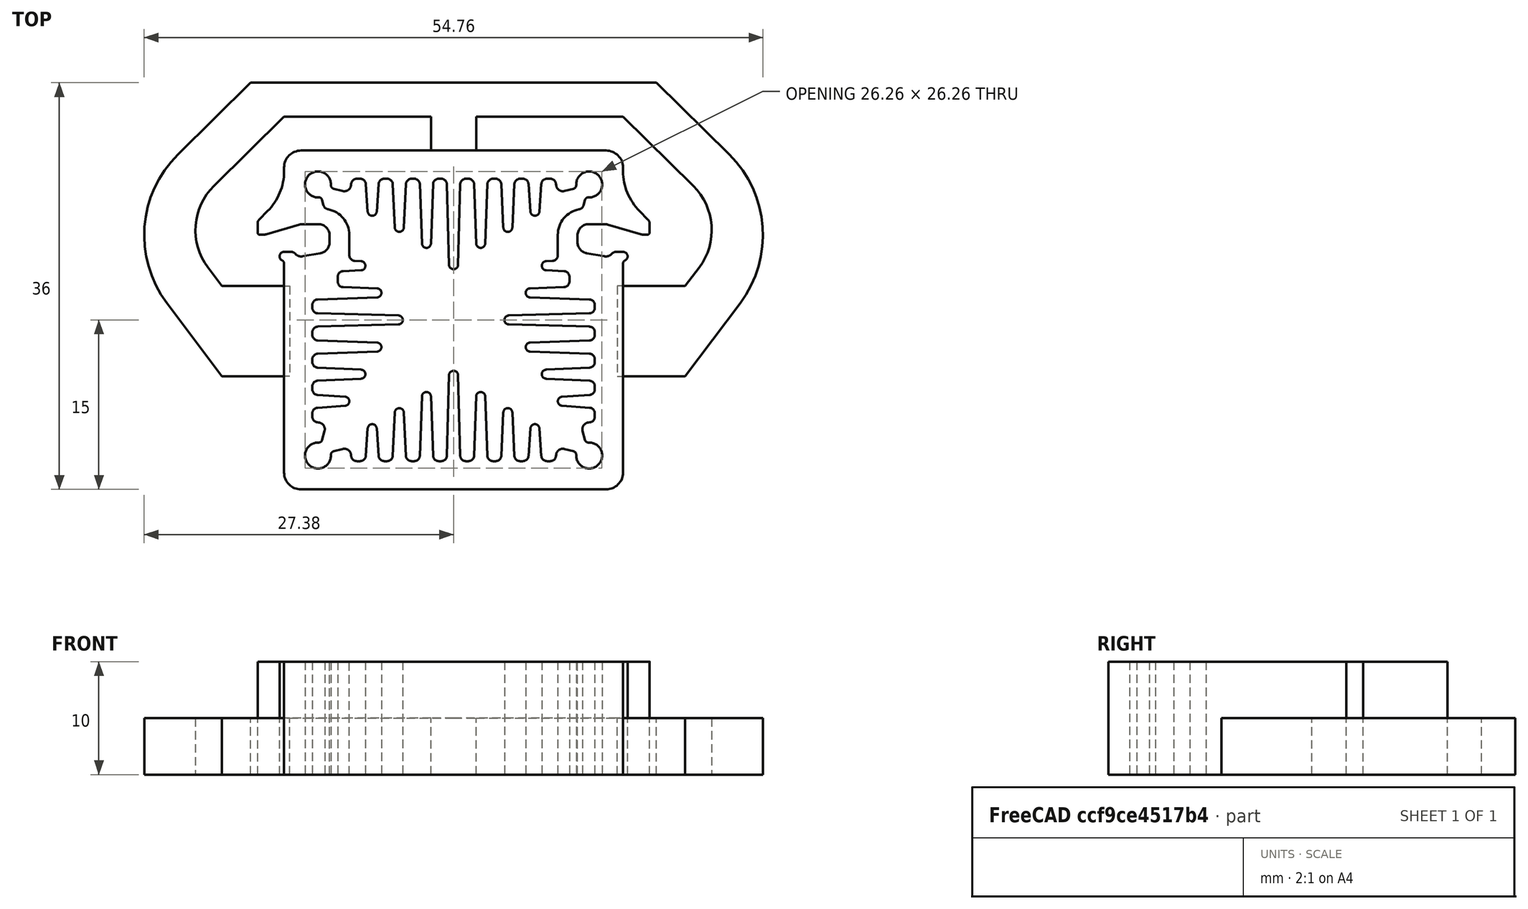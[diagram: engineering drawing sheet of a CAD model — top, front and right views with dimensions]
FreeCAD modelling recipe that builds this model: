
FCSTD DOCUMENT  (FreeCAD 0.20R29603 (Git))
Label: NTCclip
License: All rights reserved
LicenseURL: http://en.wikipedia.org/wiki/All_rights_reserved
objects: Part::Feature×1, Sketcher::SketchObject×1, PartDesign::Pad×1, PartDesign::Body×1
note: 5 computed .brp shape members not serialized (recipe doc carries the construction recipe); baked Part::Feature solids carry a one-line shape summary decoded from their .brp

FEATURE [Part::Feature] Part__Feature  label="LAM_3_K"
  shape: bbox 34.69 x 30 x 10 mm, 252 faces (baked)
FEATURE [Sketcher::SketchObject] Sketch
  FullyConstrained = false
  MapMode = 5
  Support = -> [XY_Plane]
  sketch-geometry (33):
    g0: LineSegment StartX=-14.5 StartY=3 StartZ=0 EndX=-14.5 EndY=-5 EndZ=0
    g1: LineSegment StartX=-14.5 StartY=-5 StartZ=0 EndX=-20.5 EndY=-5 EndZ=0
    g2: LineSegment StartX=-20.5 StartY=-5 StartZ=0 EndX=-25.3698 EndY=1.49312 EndZ=0
    g3: LineSegment StartX=-24.3914 StartY=14.6527 StartZ=0 EndX=-17.9605 EndY=21 EndZ=0
    g4: LineSegment StartX=-17.9605 StartY=21 StartZ=0 EndX=0 EndY=21 EndZ=0
    g5: LineSegment StartX=0 StartY=21 StartZ=0 EndX=0 EndY=15 EndZ=0
    g6: LineSegment StartX=0 StartY=15 StartZ=0 EndX=-2 EndY=15 EndZ=0
    g7: LineSegment StartX=-2 StartY=15 StartZ=0 EndX=-2 EndY=18 EndZ=0
    g8: LineSegment StartX=-2 StartY=18 StartZ=0 EndX=-15 EndY=18 EndZ=0
    g9: LineSegment StartX=-15 StartY=18 StartZ=0 EndX=-21.2076 EndY=11.8731 EndZ=0
    g10: LineSegment StartX=-21.744 StartY=4.65863 StartZ=0 EndX=-20.5 EndY=3 EndZ=0
    g11: LineSegment StartX=-20.5 StartY=3 StartZ=0 EndX=-14.5 EndY=3 EndZ=0
    g12: ArcOfCircle CenterX=-17.344 CenterY=7.95863 CenterZ=0 NormalX=0 NormalY=0 NormalZ=1 AngleXU=0 Radius=5.5 StartAngle=2.34966 EndAngle=3.78509
    g13: GeomPoint X=-24.625 Y=8.5 Z=0
    g14: ArcOfCircle CenterX=-17.344 CenterY=7.51252 CenterZ=0 NormalX=0 NormalY=0 NormalZ=1 AngleXU=0 Radius=10.0323 StartAngle=2.34966 EndAngle=3.78509
    g15: GeomPoint X=-30.625 Y=8.5 Z=0
    g16: LineSegment StartX=-30.625 StartY=8.5 StartZ=0 EndX=-24.625 EndY=8.5 EndZ=0
    g17: LineSegment StartX=14.5 StartY=3 StartZ=0 EndX=14.5 EndY=-5 EndZ=0
    g18: LineSegment StartX=14.5 StartY=-5 StartZ=0 EndX=20.5 EndY=-5 EndZ=0
    g19: LineSegment StartX=20.5 StartY=-5 StartZ=0 EndX=25.3698 EndY=1.49312 EndZ=0
    g20: LineSegment StartX=24.3914 StartY=14.6527 StartZ=0 EndX=17.9605 EndY=21 EndZ=0
    g21: LineSegment StartX=17.9605 StartY=21 StartZ=0 EndX=0 EndY=21 EndZ=0
    g22: LineSegment StartX=-2.372e-12 StartY=15 StartZ=0 EndX=2 EndY=15 EndZ=0
    g23: LineSegment StartX=2 StartY=15 StartZ=0 EndX=2 EndY=18 EndZ=0
    g24: LineSegment StartX=2 StartY=18 StartZ=0 EndX=15 EndY=18 EndZ=0
    g25: LineSegment StartX=15 StartY=18 StartZ=0 EndX=21.2076 EndY=11.8731 EndZ=0
    g26: LineSegment StartX=21.744 StartY=4.65863 StartZ=0 EndX=20.5 EndY=3 EndZ=0
    g27: LineSegment StartX=20.5 StartY=3 StartZ=0 EndX=14.5 EndY=3 EndZ=0
    g28: ArcOfCircle CenterX=17.344 CenterY=7.95863 CenterZ=0 NormalX=0 NormalY=0 NormalZ=1 AngleXU=0 Radius=5.5 StartAngle=5.63968 EndAngle=7.07512
    g29: GeomPoint X=24.625 Y=8.5 Z=0
    g30: ArcOfCircle CenterX=17.344 CenterY=7.51252 CenterZ=0 NormalX=0 NormalY=0 NormalZ=1 AngleXU=0 Radius=10.0323 StartAngle=5.63968 EndAngle=7.07512
    g31: GeomPoint X=30.625 Y=8.5 Z=0
    g32: LineSegment StartX=30.625 StartY=8.5 StartZ=0 EndX=24.625 EndY=8.5 EndZ=0
  constraints (85):
    c: Vertical(g0)
    c: Coincident(g0,g1)
    c: Horizontal(g1)
    c: Coincident(g1,g2)
    c: Coincident(g3,g4)
    c: PointOnObject(g4,g-2)
    c: Horizontal(g4)
    c: Coincident(g4,g5)
    c: PointOnObject(g5,g-2)
    c: Coincident(g5,g6)
    c: Horizontal(g6)
    c: Coincident(g6,g7)
    c: Vertical(g7)
    c: Coincident(g7,g8)
    c: Horizontal(g8)
    c: Coincident(g8,g9)
    c: Coincident(g10,g11)
    c: Coincident(g11,g0)
    c: Horizontal(g11)
    c: Equal(g11,g1)
    c: DistanceY(g-1,g5) = 15
    c: DistanceX(g0,g-1) = 14.5
    c: PointOnObject(g13,g9)
    c: PointOnObject(g13,g10)
    c: Tangent(g9,g12) = -1.5708
    c: Tangent(g10,g12) = -1.5708
    c: PointOnObject(g15,g2)
    c: PointOnObject(g15,g3)
    c: Tangent(g2,g14) = 1.5708
    c: Tangent(g3,g14) = 1.5708
    c: DistanceY(g7,g4) = 3
    c: Coincident(g16,g15)
    c: Coincident(g16,g13)
    c: Horizontal(g16)
    c: Equal(g16,g5)
    c: Equal(g11,g5)
    c: Parallel(g9,g3)
    c: Parallel(g10,g2)
    c: DistanceY(g7,g7) = 3
    c: DistanceX(g6,g5) = 2
    c: DistanceY(g0,g0) = 8
    c: DistanceY(g-1,g0) = 3
    c: DistanceX(g8,g8) = 13
    c: DistanceY(g-1,g15) = 8.5
    c: Vertical(g12,g14)
    c: Radius(g12) = 5.5
    c: Coincident(g17,g18)
    c: Coincident(g18,g19)
    c: Coincident(g20,g21)
    c: Coincident(g22,g23)
    c: Coincident(g23,g24)
    c: Coincident(g24,g25)
    c: Coincident(g26,g27)
    c: Coincident(g27,g17)
    c: Equal(g27,g18)
    c: PointOnObject(g29,g25)
    c: PointOnObject(g29,g26)
    c: Tangent(g25,g28) = 1.5708
    c: Tangent(g26,g28) = 1.5708
    c: PointOnObject(g31,g19)
    c: PointOnObject(g31,g20)
    c: Tangent(g19,g30) = -1.5708
    c: Tangent(g20,g30) = -1.5708
    c: Coincident(g32,g31)
    c: Coincident(g32,g29)
    c: Parallel(g25,g20)
    c: Parallel(g26,g19)
    c: Radius(g28) = 5.5
    c: Equal(g4,g21)
    c: Equal(g8,g24)
    c: Horizontal(g0,g17)
    c: Equal(g1,g18)
    c: Horizontal(g18)
    c: Horizontal(g27)
    c: Horizontal(g24)
    c: Horizontal(g21)
    c: Equal(g20,g3)
    c: Horizontal(g17,g0)
    c: Vertical(g17)
    c: Symmetric(g29,g13,g-2)
    c: Vertical(g23)
    c: Symmetric(g22,g6,g-2)
    c: Horizontal(g23,g7)
    c: Coincident(g21,g4)
    c: Equal(g30,g14)
FEATURE [PartDesign::Pad] Pad
  Direction = (0,0,1)
  Length = 5
  Length2 = 10
  Profile = -> Sketch
  ReferenceAxis = -> Sketch [N_Axis]
  Type = 0
FEATURE [PartDesign::Body] Body
  Group = -> [Sketch,Pad]
  Origin = -> Origin
  Tip = -> Pad
